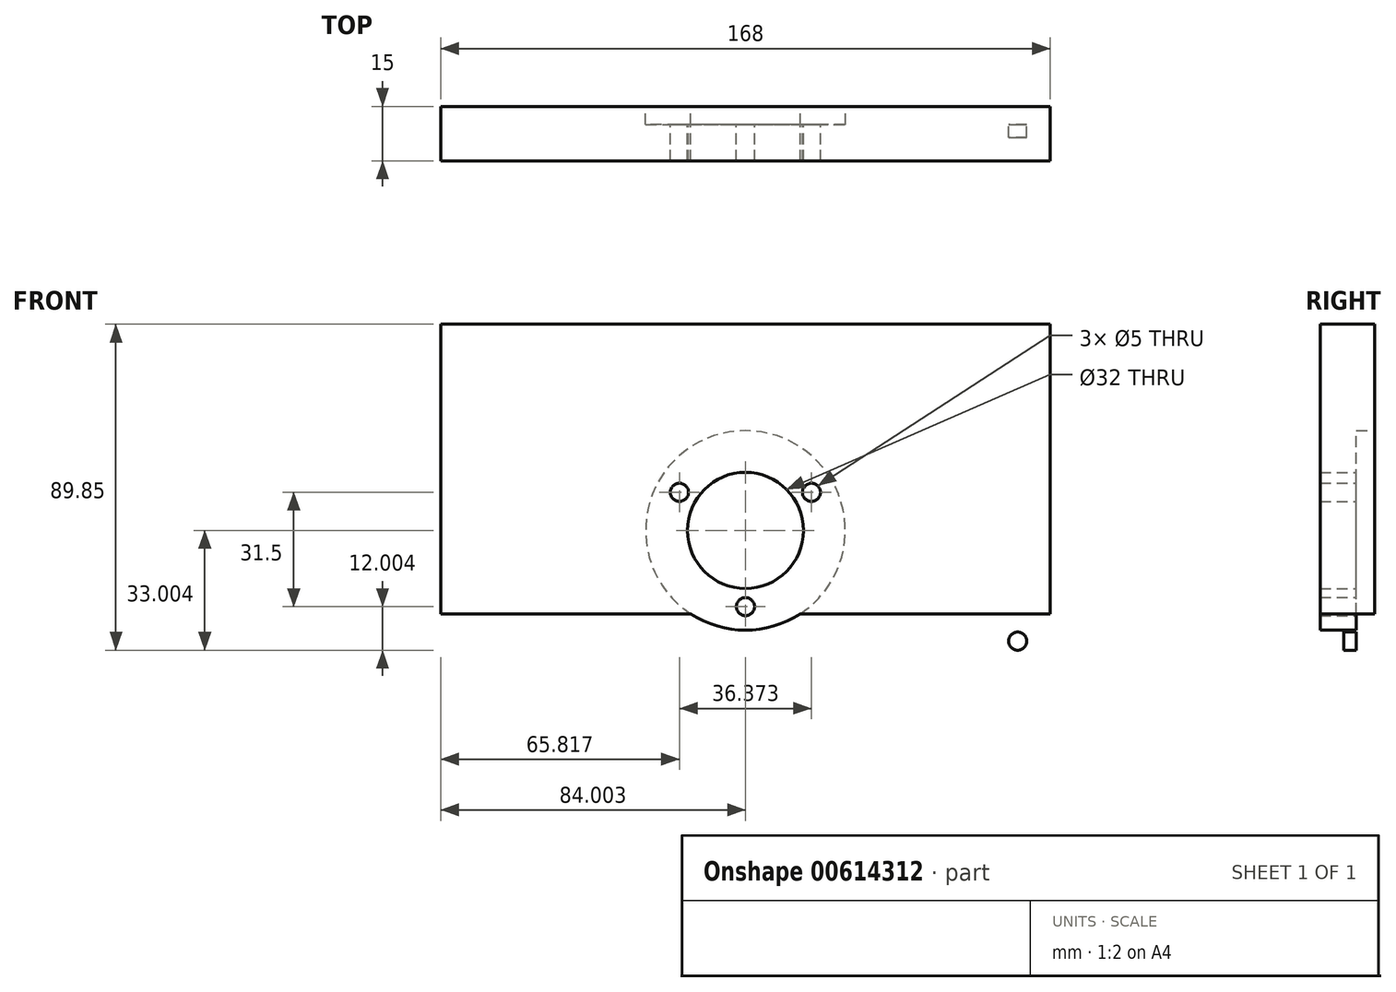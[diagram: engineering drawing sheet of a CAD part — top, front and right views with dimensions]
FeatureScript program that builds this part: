
annotation { "Feature Type Name" : "Feature", "Feature Type Description" : "" }
export const myFeature = defineFeature(function(context is Context, id is Id, definition is map)
    precondition{}
    {
        {
            var Q0;
            Q0=qCreatedBy(makeId("Front.planeOp"),FACE);
            var sketch = newSketch(context, id + "F0", { "sketchPlane" : qUnion([Q0])});
            skCircle(sketch, "E0", {"center": v(123.97, -45.53) * mm, "radius": 27.5 * mm});
            skCircle(sketch, "E1", {"center": v(123.97, -45.53) * mm, "radius": 16 * mm});
            skCircle(sketch, "E2", {"center": v(105.79, -35.03) * mm, "radius": 2.5 * mm});
            skCircle(sketch, "E3", {"center": v(123.97, -66.53) * mm, "radius": 2.5 * mm});
            skCircle(sketch, "E4", {"center": v(142.16, -35.03) * mm, "radius": 2.5 * mm});
            skLineSegment(sketch, "E5", {"start": v(123.97, -45.53) * mm, "end": v(142.16, -35.03) * mm, "construction": true});
            skCircle(sketch, "E6", {"center": v(123.97, -45.53) * mm, "radius": 21 * mm});
            skLineSegment(sketch, "E7", {"start": v(123.97, -45.53) * mm, "end": v(105.79, -35.03) * mm, "construction": true});
            skLineSegment(sketch, "E8.left", {"start": v(39.97, 11.32) * mm, "end": v(39.97, -88.84) * mm});
            skCircle(sketch, "E9.MirrorC", {"center": v(198.97, -76.03) * mm, "radius": 2.5 * mm});
            skLineSegment(sketch, "E10.MirrorCS", {"start": v(207.97, -88.84) * mm, "end": v(39.97, -88.84) * mm});
            skLineSegment(sketch, "E11", {"start": v(39.97, 11.32) * mm, "end": v(207.97, 11.32) * mm});
            skLineSegment(sketch, "E12", {"start": v(39.97, -68.53) * mm, "end": v(108.9, -68.53) * mm});
            skLineSegment(sketch, "E13", {"start": v(123.97, -45.53) * mm, "end": v(123.97, -66.53) * mm, "construction": true});
            skLineSegment(sketch, "E14", {"start": v(207.97, 11.32) * mm, "end": v(207.97, -88.84) * mm});
            skLineSegment(sketch, "E15", {"start": v(108.9, -68.53) * mm, "end": v(139.05, -68.53) * mm, "construction": true});
            skLineSegment(sketch, "E16", {"start": v(139.05, -68.53) * mm, "end": v(207.97, -68.53) * mm});
            skLineSegment(sketch, "E17", {"start": v(123.97, -66.53) * mm, "end": v(123.97, -88.84) * mm, "construction": true});
            skCircle(sketch, "E18.1.0.0", {"center": v(168.97, -76.03) * mm, "radius": 2.5 * mm});
            skCircle(sketch, "E18.2.0.0", {"center": v(138.97, -76.03) * mm, "radius": 2.5 * mm});
            skCircle(sketch, "E18.3.0.0", {"center": v(108.97, -76.03) * mm, "radius": 2.5 * mm});
            skCircle(sketch, "E18.4.0.0", {"center": v(78.97, -76.03) * mm, "radius": 2.5 * mm});
            skCircle(sketch, "E18.5.0.0", {"center": v(48.97, -76.03) * mm, "radius": 2.5 * mm});
            skLineSegment(sketch, "E18.direction1", {"start": v(198.97, -76.03) * mm, "end": v(168.97, -76.03) * mm, "construction": true});
            skSolve(sketch);
        }
        {
            var Q0;
            Q0=makeQuery(id+"F0.imprint","IMPRINT",FACE,{"disambiguationData":[TD([[makeQuery(id+"F0.imprint","IMPRINT",EDGE,{"derivedFrom":sQuery(id+"F0.wireOp",EDGE,"Le6oXkVk-5rep-NBvs-UWGL-70AeHxEeUJYF")}),-1.0]])]});
            var Q1;
            {var subQ8=sQuery(id+"F0.wireOp",EDGE,"E0");var subQ9=makeQuery(id+"F0.imprint","INTERSECT",VERTEX,{"derivedFrom":[subQ8,sQuery(id+"F0.wireOp",EDGE,"E12")]});Q1=makeQuery(id+"F0.imprint","IMPRINT",FACE,{"disambiguationData":[TD([[makeQuery(id+"F0.imprint","IMPRINT",EDGE,{"disambiguationData":[TD([[subQ9,-1.0]])],"derivedFrom":subQ8}),1.0]])]});}
            var Q2;
            Q2=makeQuery(id+"F0.imprint","IMPRINT",FACE,{"disambiguationData":[TD([[makeQuery(id+"F0.imprint","IMPRINT",EDGE,{"derivedFrom":sQuery(id+"F0.wireOp",EDGE,"E1")}),-1.0]])]});
            var Q3;
            {var subQ0=sQuery(id+"F0.wireOp",EDGE,"E11");Q3=makeQuery(id+"F0.imprint","IMPRINT",FACE,{"disambiguationData":[TD([[makeQuery(id+"F0.imprint","IMPRINT",EDGE,{"derivedFrom":subQ0}),-1.0]])]});}
            var Q4;
            Q4=makeQuery(id+"F0.imprint","IMPRINT",FACE,{"disambiguationData":[TD([[makeQuery(id+"F0.imprint","IMPRINT",EDGE,{"derivedFrom":sQuery(id+"F0.wireOp",EDGE,"E9.MirrorC")}),1.0]])]});
            extrude(context, id + "F1", {"entities" : qUnion([Q0, Q1, Q2, Q3, Q4]), "depth" : 15 * mm, "offsetDistance" : 25 * mm});
        }
        {
            var Q0;
            {var subQ8=sQuery(id+"F0.wireOp",EDGE,"E0");var subQ9=makeQuery(id+"F0.imprint","INTERSECT",VERTEX,{"derivedFrom":[subQ8,sQuery(id+"F0.wireOp",EDGE,"E12")]});Q0=makeQuery(id+"F0.imprint","IMPRINT",FACE,{"disambiguationData":[TD([[makeQuery(id+"F0.imprint","IMPRINT",EDGE,{"disambiguationData":[TD([[subQ9,-1.0]])],"derivedFrom":subQ8}),1.0]])]});}
            var Q1;
            Q1=makeQuery(id+"F0.imprint","IMPRINT",FACE,{"disambiguationData":[TD([[makeQuery(id+"F0.imprint","IMPRINT",EDGE,{"derivedFrom":sQuery(id+"F0.wireOp",EDGE,"E1")}),-1.0]])]});
            var Q2;
            Q2=makeQuery(id+"F0.imprint","IMPRINT",FACE,{"disambiguationData":[TD([[makeQuery(id+"F0.imprint","IMPRINT",EDGE,{"derivedFrom":sQuery(id+"F0.wireOp",EDGE,"E9.MirrorC")}),1.0]])]});
            extrude(context, id + "F2", {"entities" : qUnion([Q0, Q1, Q2]), "operationType" : NewBodyOperationType.REMOVE, "depth" : 5 * mm, "offsetDistance" : 25 * mm});
        }
        {
            var Q0;
            Q0=makeQuery(id+"F1.opExtrude","CAP_FACE",FACE,{"disambiguationData":[OSD([sQuery(id+"F0.wireOp",EDGE,"E1"),sQuery(id+"F0.wireOp",EDGE,"E2"),sQuery(id+"F0.wireOp",EDGE,"E3"),sQuery(id+"F0.wireOp",EDGE,"E4"),sQuery(id+"F0.wireOp",EDGE,"E8.left"),sQuery(id+"F0.wireOp",EDGE,"Le6oXkVk-5rep-NBvs-UWGL-70AeHxEeUJYF"),sQuery(id+"F0.wireOp",EDGE,"E9.MirrorC"),sQuery(id+"F0.wireOp",EDGE,"E10.MirrorCS"),sQuery(id+"F0.wireOp",EDGE,"E11"),sQuery(id+"F0.wireOp",EDGE,"E14")])],"isStart":false});
            var sketch = newSketch(context, id + "F3", { "sketchPlane" : qUnion([Q0])});
            skCircle(sketch, "E19", {"center": v(198.97, -76.03) * mm, "radius": 5.5 * mm});
            skCircle(sketch, "E20", {"center": v(168.97, -76.03) * mm, "radius": 5.5 * mm});
            skCircle(sketch, "E21", {"center": v(138.97, -76.03) * mm, "radius": 5.5 * mm});
            skCircle(sketch, "E22", {"center": v(108.97, -76.03) * mm, "radius": 5.5 * mm});
            skCircle(sketch, "E23", {"center": v(78.97, -76.03) * mm, "radius": 5.5 * mm});
            skCircle(sketch, "E24", {"center": v(48.97, -76.03) * mm, "radius": 5.5 * mm});
            skSolve(sketch);
        }
        {
            var Q0;
            Q0=makeQuery(id+"F3.imprint","IMPRINT",FACE,{"disambiguationData":[TD([[makeQuery(id+"F3.imprint","IMPRINT",EDGE,{"derivedFrom":sQuery(id+"F3.wireOp",EDGE,"Wk3q93wI-sA6F-m8JS-RqMK-6r4YREosQJEW")}),1.0]])]});
            var Q1;
            Q1=makeQuery(id+"F3.imprint","IMPRINT",FACE,{"disambiguationData":[TD([[makeQuery(id+"F3.imprint","IMPRINT",EDGE,{"derivedFrom":sQuery(id+"F3.wireOp",EDGE,"E19")}),1.0]])]});
            var Q2;
            Q2=makeQuery(id+"F3.imprint","IMPRINT",FACE,{"disambiguationData":[TD([[makeQuery(id+"F3.imprint","IMPRINT",EDGE,{"derivedFrom":sQuery(id+"F3.wireOp",EDGE,"E20")}),1.0]])]});
            var Q3;
            Q3=makeQuery(id+"F3.imprint","IMPRINT",FACE,{"disambiguationData":[TD([[makeQuery(id+"F3.imprint","IMPRINT",EDGE,{"derivedFrom":sQuery(id+"F3.wireOp",EDGE,"E21")}),1.0]])]});
            var Q4;
            Q4=makeQuery(id+"F3.imprint","IMPRINT",FACE,{"disambiguationData":[TD([[makeQuery(id+"F3.imprint","IMPRINT",EDGE,{"derivedFrom":sQuery(id+"F3.wireOp",EDGE,"E22")}),1.0]])]});
            var Q5;
            Q5=makeQuery(id+"F3.imprint","IMPRINT",FACE,{"disambiguationData":[TD([[makeQuery(id+"F3.imprint","IMPRINT",EDGE,{"derivedFrom":sQuery(id+"F3.wireOp",EDGE,"E23")}),1.0]])]});
            var Q6;
            Q6=makeQuery(id+"F3.imprint","IMPRINT",FACE,{"disambiguationData":[TD([[makeQuery(id+"F3.imprint","IMPRINT",EDGE,{"derivedFrom":sQuery(id+"F3.wireOp",EDGE,"E24")}),1.0]])]});
            extrude(context, id + "F4", {"entities" : qUnion([Q0, Q1, Q2, Q3, Q4, Q5, Q6]), "operationType" : NewBodyOperationType.REMOVE, "oppositeDirection" : true, "depth" : 6.5 * mm, "offsetDistance" : 25 * mm});
        }
    });
